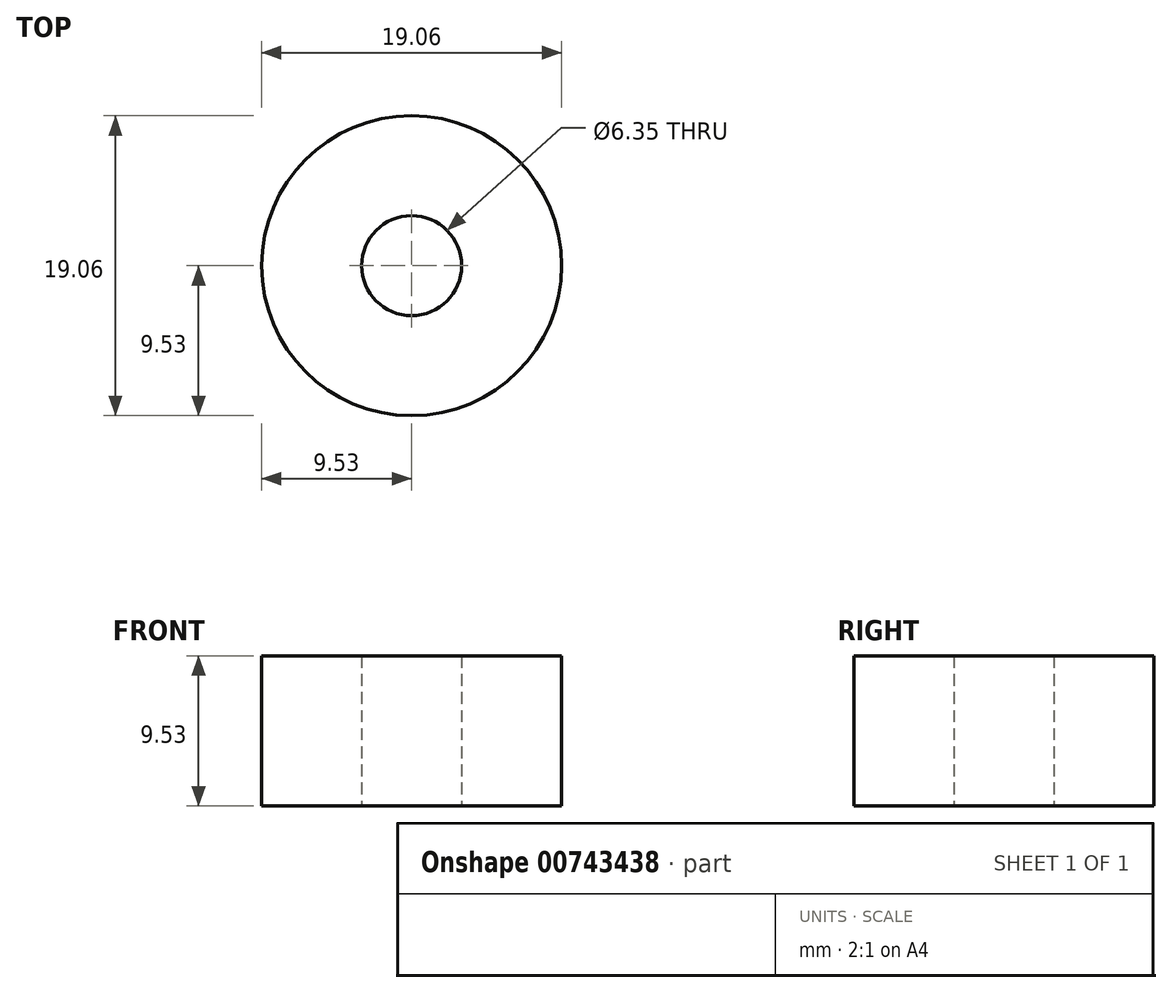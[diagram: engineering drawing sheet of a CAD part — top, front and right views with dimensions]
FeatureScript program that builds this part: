
annotation { "Feature Type Name" : "Feature", "Feature Type Description" : "" }
export const myFeature = defineFeature(function(context is Context, id is Id, definition is map)
    precondition{}
    {
        {
            var Q0;
            Q0=qCreatedBy(makeId("Top.planeOp"),FACE);
            var sketch = newSketch(context, id + "F0", { "sketchPlane" : qUnion([Q0])});
            skCircle(sketch, "E0", {"center": v(0, 0) * mm, "radius": 9.53 * mm});
            skCircle(sketch, "E1", {"center": v(0, 0) * mm, "radius": 3.17 * mm});
            skSolve(sketch);
        }
        {
            var Q0;
            Q0=makeQuery(id+"F0.imprint","IMPRINT",FACE,{"disambiguationData":[TD([[makeQuery(id+"F0.imprint","IMPRINT",EDGE,{"derivedFrom":sQuery(id+"F0.wireOp",EDGE,"E0")}),1.0]])]});
            extrude(context, id + "F1", {"entities" : qUnion([Q0]), "depth" : 9.52 * mm, "offsetDistance" : 25.4 * mm});
        }
    });
